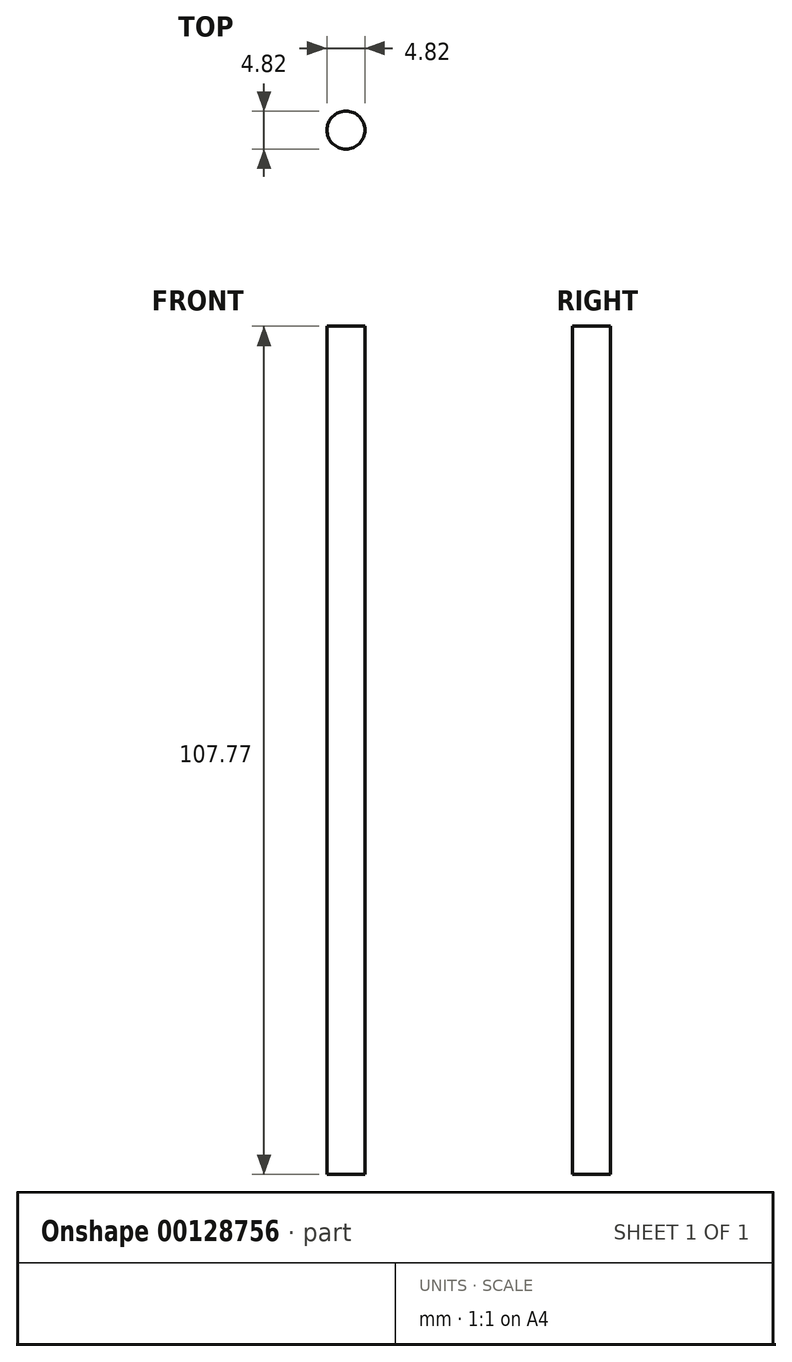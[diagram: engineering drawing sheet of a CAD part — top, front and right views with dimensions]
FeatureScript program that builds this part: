
annotation { "Feature Type Name" : "Feature", "Feature Type Description" : "" }
export const myFeature = defineFeature(function(context is Context, id is Id, definition is map)
    precondition{}
    {
        {
            var Q0;
            Q0=qCreatedBy(makeId("Top.planeOp"),FACE);
            var sketch = newSketch(context, id + "F0", { "sketchPlane" : qUnion([Q0])});
            skCircle(sketch, "E0", {"center": v(0, 0) * mm, "radius": 2.41 * mm});
            skSolve(sketch);
        }
        {
            var Q0;
            Q0 = qSketchRegion(id + "F0", true);
            extrude(context, id + "F1", {"entities" : qUnion([Q0]), "depth" : 107.77 * mm});
        }
    });
